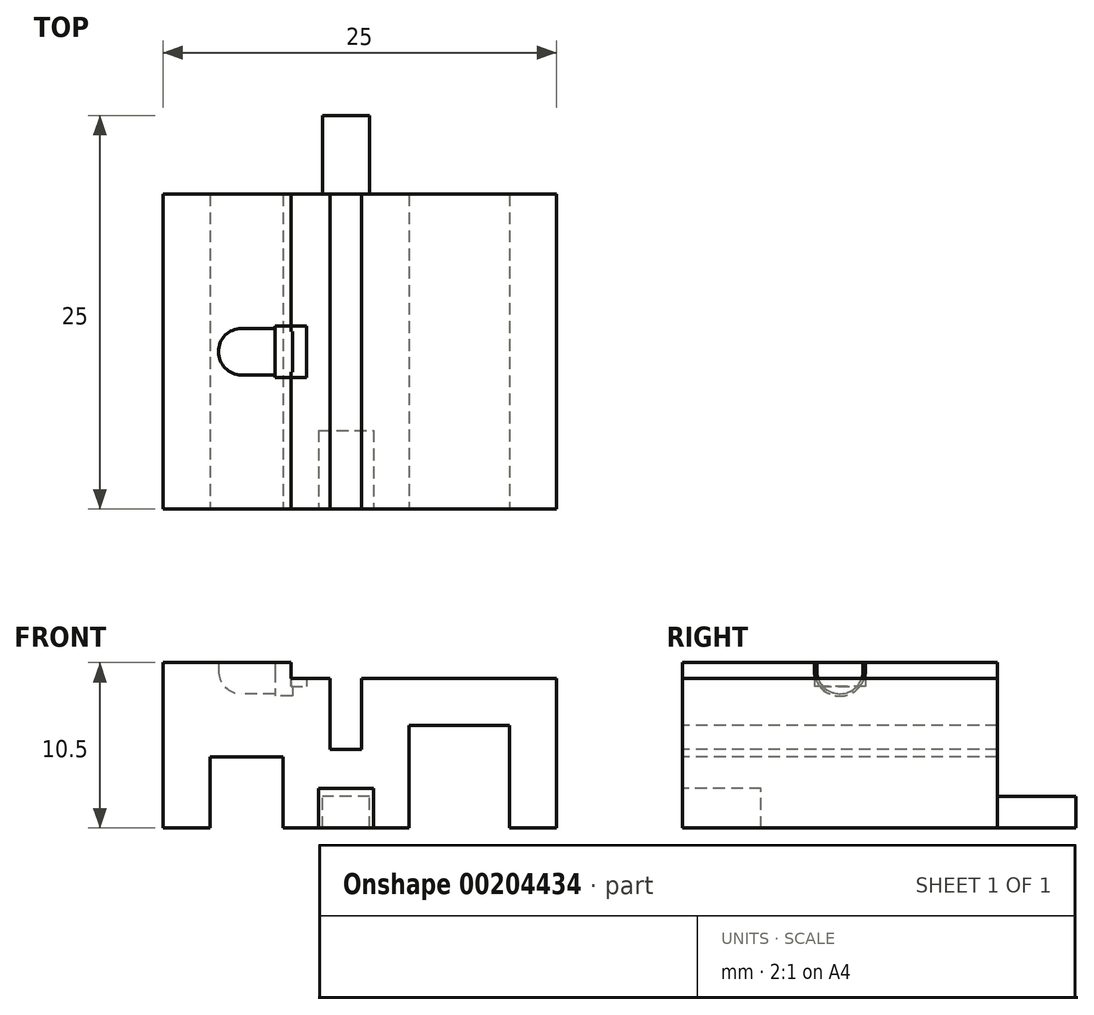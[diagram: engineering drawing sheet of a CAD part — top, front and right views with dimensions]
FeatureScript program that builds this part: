
annotation { "Feature Type Name" : "Feature", "Feature Type Description" : "" }
export const myFeature = defineFeature(function(context is Context, id is Id, definition is map)
    precondition{}
    {
        {
            var Q0;
            Q0=qCreatedBy(makeId("Top.planeOp"),FACE);
            var sketch = newSketch(context, id + "F0", { "sketchPlane" : qUnion([Q0])});
            skLineSegment(sketch, "E0.bottom", {"start": v(-5, 10) * mm, "end": v(20, 10) * mm});
            skLineSegment(sketch, "E0.top", {"start": v(-5, -10) * mm, "end": v(20, -10) * mm});
            skLineSegment(sketch, "E0.left", {"start": v(-5, 10) * mm, "end": v(-5, -10) * mm});
            skLineSegment(sketch, "E0.right", {"start": v(20, 10) * mm, "end": v(20, -10) * mm});
            skSolve(sketch);
        }
        {
            var Q0;
            Q0 = qSketchRegion(id + "F0", true);
            extrude(context, id + "F1", {"entities" : qUnion([Q0]), "oppositeDirection" : true, "depth" : 10 * mm});
        }
        {
            var Q0;
            Q0=qCreatedBy(makeId("Top.planeOp"),FACE);
            var sketch = newSketch(context, id + "F2", { "sketchPlane" : qUnion([Q0])});
            skArc(sketch, "E1", {"start": v(-1.48, 0) * mm, "mid": v(-1.04, -1.04) * mm, "end": v(0, -1.48) * mm});
            skLineSegment(sketch, "E2", {"start": v(0, -1.48) * mm, "end": v(2.12, -1.48) * mm});
            skLineSegment(sketch, "E3", {"start": v(2.12, -1.47) * mm, "end": v(2.12, -1.62) * mm});
            skLineSegment(sketch, "E4", {"start": v(2.13, -1.62) * mm, "end": v(3.23, -1.62) * mm});
            skLineSegment(sketch, "E5", {"start": v(3.23, -1.62) * mm, "end": v(3.23, 0) * mm});
            skLineSegment(sketch, "E6", {"start": v(3.23, 0) * mm, "end": v(-1.48, 0) * mm});
            skLineSegment(sketch, "E7", {"start": v(-1.48, 0) * mm, "end": v(-4.24, 0) * mm, "construction": true});
            skSolve(sketch);
        }
        {
            var Q0;
            Q0 = qSketchRegion(id + "F2", true);
            var Q1;
            Q1=sQuery(id+"F2.wireOp",EDGE,"E7");
            revolve(context, id + "F3", {"operationType" : NewBodyOperationType.REMOVE, "entities" : qUnion([Q0]), "axis" : qUnion([Q1]), "revolveType" : RevolveType.FULL, "oppositeDirection" : true});
        }
        {
            var Q0;
            Q0=qCreatedBy(makeId("Front.planeOp"),FACE);
            var sketch = newSketch(context, id + "F4", { "sketchPlane" : qUnion([Q0])});
            skLineSegment(sketch, "E8", {"start": v(0, 0) * mm, "end": v(3.13, 0) * mm, "construction": true});
            skLineSegment(sketch, "E9.bottom", {"start": v(3.13, 0) * mm, "end": v(4.13, 0) * mm});
            skLineSegment(sketch, "E9.top", {"start": v(3.13, -1) * mm, "end": v(4.13, -1) * mm});
            skLineSegment(sketch, "E9.left", {"start": v(3.13, 0) * mm, "end": v(3.13, -1) * mm});
            skLineSegment(sketch, "E9.right", {"start": v(4.13, 0) * mm, "end": v(4.13, -1) * mm});
            skLineSegment(sketch, "E10", {"start": v(3.13, 0) * mm, "end": v(5.63, 0) * mm});
            skLineSegment(sketch, "E11", {"start": v(5.63, 0) * mm, "end": v(7.63, 0) * mm});
            skLineSegment(sketch, "E12.top", {"start": v(5.63, -5) * mm, "end": v(7.63, -5) * mm});
            skLineSegment(sketch, "E12.left", {"start": v(5.63, 0) * mm, "end": v(5.63, -5) * mm});
            skLineSegment(sketch, "E12.right", {"start": v(7.63, 0) * mm, "end": v(7.63, -5) * mm});
            skSolve(sketch);
        }
        {
            var Q0;
            Q0 = qSketchRegion(id + "F4", true);
            extrude(context, id + "F5", {"entities" : qUnion([Q0]), "operationType" : NewBodyOperationType.REMOVE, "oppositeDirection" : true, "depth" : 25 * mm, "hasSecondDirection" : true, "secondDirectionOppositeDirection" : false, "secondDirectionDepth" : 25 * mm});
        }
        {
            var Q0;
            {var subQ0=sQuery(id+"F0.wireOp",EDGE,"E0.bottom");var subQ1=sQuery(id+"F0.wireOp",EDGE,"E0.top");Q0=makeQuery(id+"F5.boolean.opBoolean","SPLIT",FACE,{"disambiguationData":[TD([makeQuery(id+"F5.opExtrude","SWEPT_FACE",FACE,{"disambiguationData":[OSD([sQuery(id+"F4.wireOp",EDGE,"E9.right")])]})])],"derivedFrom":makeQuery(id+"F1.opExtrude","CAP_FACE",FACE,{"disambiguationData":[OSD([subQ0,subQ1,sQuery(id+"F0.wireOp",EDGE,"E0.left"),sQuery(id+"F0.wireOp",EDGE,"E0.right")])],"isStart":true})});}
            var Q1;
            {var subQ0=sQuery(id+"F0.wireOp",EDGE,"E0.bottom");var subQ1=sQuery(id+"F0.wireOp",EDGE,"E0.top");var subQ2=sQuery(id+"F0.wireOp",EDGE,"E0.right");Q1=makeQuery(id+"F5.boolean.opBoolean","SPLIT",FACE,{"disambiguationData":[TD([makeQuery(id+"F1.opExtrude","SWEPT_FACE",FACE,{"disambiguationData":[OSD([subQ2])]})])],"derivedFrom":makeQuery(id+"F1.opExtrude","CAP_FACE",FACE,{"disambiguationData":[OSD([subQ0,subQ1,sQuery(id+"F0.wireOp",EDGE,"E0.left"),subQ2])],"isStart":true})});}
            extrude(context, id + "F6", {"entities" : qUnion([Q0, Q1]), "operationType" : NewBodyOperationType.REMOVE, "oppositeDirection" : true, "depth" : 0.5 * mm});
        }
        {
            var Q0;
            {var subQ0=sQuery(id+"F0.wireOp",EDGE,"E0.left");var subQ1=sQuery(id+"F0.wireOp",EDGE,"E0.top");var subQ2=sQuery(id+"F0.wireOp",EDGE,"E0.bottom");Q0=makeQuery(id+"F5.boolean.opBoolean","SPLIT",FACE,{"disambiguationData":[TD([makeQuery(id+"F1.opExtrude","SWEPT_FACE",FACE,{"disambiguationData":[OSD([subQ0])]})])],"derivedFrom":makeQuery(id+"F1.opExtrude","CAP_FACE",FACE,{"disambiguationData":[OSD([subQ2,subQ1,subQ0,sQuery(id+"F0.wireOp",EDGE,"E0.right")])],"isStart":true})});}
            extrude(context, id + "F7", {"entities" : qUnion([Q0]), "operationType" : NewBodyOperationType.ADD, "depth" : 0.5 * mm});
        }
        {
            var Q0;
            {var subQ0=sQuery(id+"F0.wireOp",EDGE,"E0.top");Q0=makeQuery(id+"F7.boolean.opBoolean","MERGE",FACE,{"derivedFrom":[makeQuery(id+"F1.opExtrude","SWEPT_FACE",FACE,{"disambiguationData":[OSD([subQ0])]}),makeQuery(id+"F7.opExtrude","SWEPT_FACE",FACE,{"disambiguationData":[OSD([subQ0])]})]});}
            var sketch = newSketch(context, id + "F8", { "sketchPlane" : qUnion([Q0])});
            skLineSegment(sketch, "E13.bottom", {"start": v(-2, -10) * mm, "end": v(2.63, -10) * mm});
            skLineSegment(sketch, "E13.top", {"start": v(-2, -5.5) * mm, "end": v(2.63, -5.5) * mm});
            skLineSegment(sketch, "E13.left", {"start": v(-2, -10) * mm, "end": v(-2, -5.5) * mm});
            skLineSegment(sketch, "E13.right", {"start": v(2.63, -10) * mm, "end": v(2.63, -5.5) * mm});
            skLineSegment(sketch, "E14.bottom", {"start": v(10.63, -3.5) * mm, "end": v(17, -3.5) * mm});
            skLineSegment(sketch, "E14.top", {"start": v(10.63, -10) * mm, "end": v(17, -10) * mm});
            skLineSegment(sketch, "E14.left", {"start": v(10.63, -3.5) * mm, "end": v(10.63, -10) * mm});
            skLineSegment(sketch, "E14.right", {"start": v(17, -3.5) * mm, "end": v(17, -10) * mm});
            skSolve(sketch);
        }
        {
            var Q0;
            Q0 = qSketchRegion(id + "F8", true);
            extrude(context, id + "F9", {"entities" : qUnion([Q0]), "operationType" : NewBodyOperationType.REMOVE, "oppositeDirection" : true, "depth" : 25 * mm});
        }
        {
            var Q0;
            Q0=makeQuery(id+"F5.boolean.opBoolean","COPY",FACE,{"derivedFrom":makeQuery(id+"F5.opExtrude","SWEPT_FACE",FACE,{"disambiguationData":[OSD([sQuery(id+"F4.wireOp",EDGE,"E9.top")])]})});
            var sketch = newSketch(context, id + "F10", { "sketchPlane" : qUnion([Q0])});
            skLineSegment(sketch, "E15.bottom", {"start": v(3.13, -1.62) * mm, "end": v(4.13, -1.62) * mm});
            skLineSegment(sketch, "E15.top", {"start": v(3.13, -10) * mm, "end": v(4.13, -10) * mm});
            skLineSegment(sketch, "E15.left", {"start": v(3.13, -1.62) * mm, "end": v(3.13, -10) * mm});
            skLineSegment(sketch, "E15.right", {"start": v(4.13, -1.62) * mm, "end": v(4.13, -10) * mm});
            skLineSegment(sketch, "E16.bottom", {"start": v(3.13, 1.62) * mm, "end": v(4.13, 1.62) * mm});
            skLineSegment(sketch, "E16.top", {"start": v(3.13, 10) * mm, "end": v(4.13, 10) * mm});
            skLineSegment(sketch, "E16.left", {"start": v(3.13, 1.62) * mm, "end": v(3.13, 10) * mm});
            skLineSegment(sketch, "E16.right", {"start": v(4.13, 1.62) * mm, "end": v(4.13, 10) * mm});
            skSolve(sketch);
        }
        {
            var Q0;
            Q0 = qSketchRegion(id + "F10", true);
            extrude(context, id + "F11", {"entities" : qUnion([Q0]), "operationType" : NewBodyOperationType.ADD, "depth" : 0.5 * mm});
        }
        {
            var Q0;
            {var subQ0=sQuery(id+"F0.wireOp",EDGE,"E0.top");Q0=makeQuery(id+"F11.boolean.opBoolean","MERGE",FACE,{"derivedFrom":[makeQuery(id+"F7.boolean.opBoolean","MERGE",FACE,{"derivedFrom":[makeQuery(id+"F1.opExtrude","SWEPT_FACE",FACE,{"disambiguationData":[OSD([subQ0])]}),makeQuery(id+"F7.opExtrude","SWEPT_FACE",FACE,{"disambiguationData":[OSD([subQ0])]})]}),makeQuery(id+"F11.opExtrude","SWEPT_FACE",FACE,{"disambiguationData":[OSD([sQuery(id+"F10.wireOp",EDGE,"E15.top")])]})]});}
            var sketch = newSketch(context, id + "F12", { "sketchPlane" : qUnion([Q0])});
            skLineSegment(sketch, "E17.bottom", {"start": v(4.88, -10) * mm, "end": v(8.38, -10) * mm});
            skLineSegment(sketch, "E17.top", {"start": v(4.88, -7.5) * mm, "end": v(8.38, -7.5) * mm});
            skLineSegment(sketch, "E17.left", {"start": v(4.88, -10) * mm, "end": v(4.88, -7.5) * mm});
            skLineSegment(sketch, "E17.right", {"start": v(8.38, -10) * mm, "end": v(8.38, -7.5) * mm});
            skLineSegment(sketch, "E18", {"start": v(6.63, -10) * mm, "end": v(6.63, -7.5) * mm, "construction": true});
            skSolve(sketch);
        }
        {
            var Q0;
            Q0 = qSketchRegion(id + "F12", true);
            extrude(context, id + "F13", {"entities" : qUnion([Q0]), "operationType" : NewBodyOperationType.REMOVE, "oppositeDirection" : true, "depth" : 5 * mm});
        }
        {
            var Q0;
            {var subQ0=sQuery(id+"F0.wireOp",EDGE,"E0.bottom");Q0=makeQuery(id+"F11.boolean.opBoolean","MERGE",FACE,{"derivedFrom":[makeQuery(id+"F7.boolean.opBoolean","MERGE",FACE,{"derivedFrom":[makeQuery(id+"F1.opExtrude","SWEPT_FACE",FACE,{"disambiguationData":[OSD([subQ0])]}),makeQuery(id+"F7.opExtrude","SWEPT_FACE",FACE,{"disambiguationData":[OSD([subQ0])]})]}),makeQuery(id+"F11.opExtrude","SWEPT_FACE",FACE,{"disambiguationData":[OSD([sQuery(id+"F10.wireOp",EDGE,"E16.top")])]})]});}
            var sketch = newSketch(context, id + "F14", { "sketchPlane" : qUnion([Q0])});
            skLineSegment(sketch, "E19", {"start": v(-6.63, -10) * mm, "end": v(-6.63, -8) * mm, "construction": true});
            skLineSegment(sketch, "E20.bottom", {"start": v(-8.13, -10) * mm, "end": v(-5.13, -10) * mm});
            skLineSegment(sketch, "E20.top", {"start": v(-8.13, -8) * mm, "end": v(-5.13, -8) * mm});
            skLineSegment(sketch, "E20.left", {"start": v(-8.13, -10) * mm, "end": v(-8.13, -8) * mm});
            skLineSegment(sketch, "E20.right", {"start": v(-5.13, -10) * mm, "end": v(-5.13, -8) * mm});
            skSolve(sketch);
        }
        {
            var Q0;
            Q0 = qSketchRegion(id + "F14", true);
            extrude(context, id + "F15", {"entities" : qUnion([Q0]), "operationType" : NewBodyOperationType.ADD, "depth" : 5 * mm});
        }
    });
